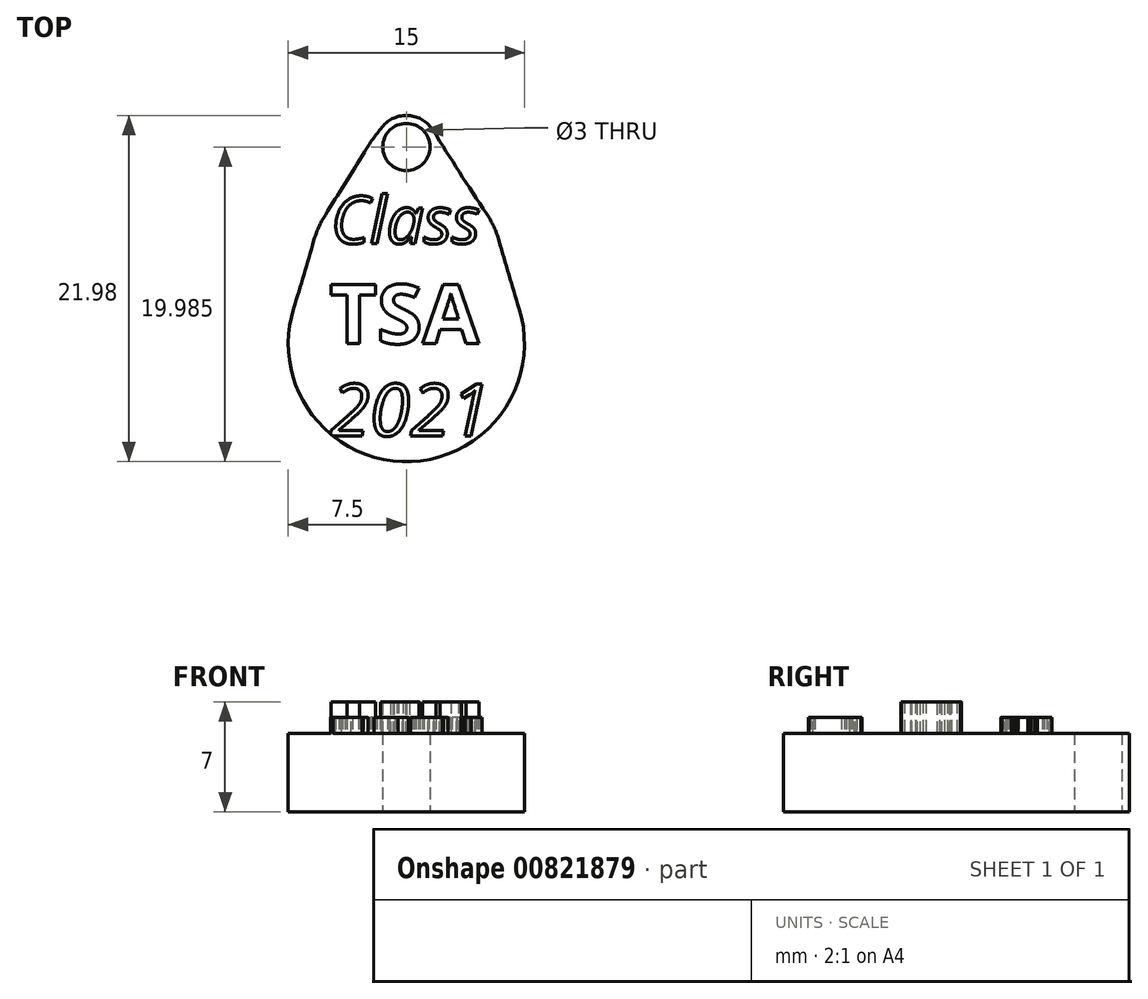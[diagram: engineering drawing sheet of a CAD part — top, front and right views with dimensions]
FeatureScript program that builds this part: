
annotation { "Feature Type Name" : "Feature", "Feature Type Description" : "" }
export const myFeature = defineFeature(function(context is Context, id is Id, definition is map)
    precondition{}
    {
        {
            var Q0;
            Q0=qCreatedBy(makeId("Top.planeOp"),FACE);
            var sketch = newSketch(context, id + "F0", { "sketchPlane" : qUnion([Q0])});
            skCircle(sketch, "E0", {"center": v(0, 0) * mm, "radius": 7.5 * mm});
            skText(sketch, "E1", { "text": "Class", "fontName": "OpenSans-Italic.ttf"});
            skLineSegment(sketch, "E2", {"start": v(-6.1, 4.38) * mm, "end": v(6.1, 4.38) * mm});
            skArc(sketch, "E3", {"start": v(6.1, 4.38) * mm, "mid": v(0, 10.98) * mm, "end": v(-6.1, 4.38) * mm});
            skCircle(sketch, "E4", {"center": v(0, 12.48) * mm, "radius": 1.5 * mm});
            skPoint(sketch, "E4.centerSnap0", {"position": v(0, 10.98) * mm});
            skCircle(sketch, "E5", {"center": v(0, 12.48) * mm, "radius": 2 * mm});
            skArc(sketch, "E6", {"start": v(-1.54, 13.76) * mm, "mid": v(-2.88, 11.78) * mm, "end": v(-3.87, 9.6) * mm});
            skLineSegment(sketch, "E7", {"start": v(0, 12.48) * mm, "end": v(0, 16.89) * mm});
            skArc(sketch, "E8.MirrorCS", {"start": v(1.54, 13.76) * mm, "mid": v(2.88, 11.78) * mm, "end": v(3.87, 9.6) * mm});
            skText(sketch, "E9", { "text": "2021", "fontName": "OpenSans-Italic.ttf"});
            const initialGuessF0  = {"E1": [-0.00479, 0.00635, 1, 0, 0.00302], "E9": [-0.00487, -0.00587, 1, 0, 0.00333]};
            skSetInitialGuess(sketch, initialGuessF0);
            skSolve(sketch);
        }
        {
            var Q0;
            {var subQ47=sQuery(id+"F0.wireOp",EDGE,"E1.sketch_text.stroke-5");Q0=makeQuery(id+"F0.imprint","IMPRINT",FACE,{"disambiguationData":[TD([[makeQuery(id+"F0.imprint","IMPRINT",EDGE,{"derivedFrom":subQ47}),1.0]])]});}
            var Q1;
            {var subQ0=sQuery(id+"F0.wireOp",EDGE,"4cedd241-6937-41b7-ad6b-732669d0c963.sketch_text.stroke-32");Q1=makeQuery(id+"F0.imprint","IMPRINT",FACE,{"disambiguationData":[TD([[makeQuery(id+"F0.imprint","IMPRINT",EDGE,{"derivedFrom":subQ0}),1.0]])]});}
            var Q2;
            {var subQ0=sQuery(id+"F0.wireOp",EDGE,"4cedd241-6937-41b7-ad6b-732669d0c963.sketch_text.stroke-5");Q2=makeQuery(id+"F0.imprint","IMPRINT",FACE,{"disambiguationData":[TD([[makeQuery(id+"F0.imprint","IMPRINT",EDGE,{"derivedFrom":subQ0}),1.0]])]});}
            var Q3;
            {var subQ21=sQuery(id+"F0.wireOp",EDGE,"4cedd241-6937-41b7-ad6b-732669d0c963.sketch_text.stroke-12");Q3=makeQuery(id+"F0.imprint","IMPRINT",FACE,{"disambiguationData":[TD([[makeQuery(id+"F0.imprint","IMPRINT",EDGE,{"derivedFrom":subQ21}),1.0]])]});}
            var Q4;
            Q4=makeQuery(id+"F0.imprint","IMPRINT",FACE,{"disambiguationData":[TD([[makeQuery(id+"F0.imprint","IMPRINT",EDGE,{"derivedFrom":sQuery(id+"F0.wireOp",EDGE,"E1.sketch_text.stroke-0")}),1.0]])]});
            var Q5;
            Q5=makeQuery(id+"F0.imprint","IMPRINT",FACE,{"disambiguationData":[TD([[makeQuery(id+"F0.imprint","IMPRINT",EDGE,{"derivedFrom":sQuery(id+"F0.wireOp",EDGE,"E1.sketch_text.stroke-36")}),1.0]])]});
            var Q6;
            {var subQ0=sQuery(id+"F0.wireOp",EDGE,"E1.sketch_text.stroke-39");Q6=makeQuery(id+"F0.imprint","IMPRINT",FACE,{"disambiguationData":[TD([[makeQuery(id+"F0.imprint","IMPRINT",EDGE,{"derivedFrom":subQ0}),1.0]])]});}
            var Q7;
            {var subQ0=sQuery(id+"F0.wireOp",EDGE,"E6");Q7=makeQuery(id+"F0.imprint","IMPRINT",FACE,{"disambiguationData":[TD([[makeQuery(id+"F0.imprint","IMPRINT",EDGE,{"derivedFrom":subQ0}),1.0]])]});}
            var Q8;
            {var subQ0=sQuery(id+"F0.wireOp",EDGE,"E8.MirrorCS");Q8=makeQuery(id+"F0.imprint","IMPRINT",FACE,{"disambiguationData":[TD([[makeQuery(id+"F0.imprint","IMPRINT",EDGE,{"derivedFrom":subQ0}),-1.0]])]});}
            var Q9;
            {var subQ0=sQuery(id+"F0.wireOp",EDGE,"E5");var subQ1=sQuery(id+"F0.wireOp",EDGE,"E3");var subQ2=makeQuery(id+"F0.imprint","INTERSECT",VERTEX,{"disambiguationData":[OD(0.0)],"derivedFrom":[subQ1,subQ0]});Q9=makeQuery(id+"F0.imprint","IMPRINT",FACE,{"disambiguationData":[TD([[makeQuery(id+"F0.imprint","IMPRINT",EDGE,{"disambiguationData":[TD([[subQ2,-1.0]])],"derivedFrom":subQ1}),1.0]])]});}
            var Q10;
            {var subQ0=sQuery(id+"F0.wireOp",EDGE,"E5");var subQ4=sQuery(id+"F0.wireOp",EDGE,"E3");var subQ5=makeQuery(id+"F0.imprint","INTERSECT",VERTEX,{"disambiguationData":[OD(0.0)],"derivedFrom":[subQ4,subQ0]});Q10=makeQuery(id+"F0.imprint","IMPRINT",FACE,{"disambiguationData":[TD([[makeQuery(id+"F0.imprint","IMPRINT",EDGE,{"disambiguationData":[TD([[subQ5,-1.0]])],"derivedFrom":subQ4}),-1.0]])]});}
            var Q11;
            {var subQ2=sQuery(id+"F0.wireOp",EDGE,"E3");var subQ6=sQuery(id+"F0.wireOp",EDGE,"E4");var subQ8=makeQuery(id+"F0.imprint","INTERSECT",VERTEX,{"derivedFrom":[subQ2,subQ6]});Q11=makeQuery(id+"F0.imprint","IMPRINT",FACE,{"disambiguationData":[TD([[makeQuery(id+"F0.imprint","IMPRINT",EDGE,{"disambiguationData":[TD([[subQ8,-1.0]])],"derivedFrom":subQ2}),-1.0]])]});}
            var Q12;
            {var subQ5=sQuery(id+"F0.wireOp",EDGE,"E2");Q12=makeQuery(id+"F0.imprint","IMPRINT",FACE,{"disambiguationData":[TD([[makeQuery(id+"F0.imprint","IMPRINT",EDGE,{"derivedFrom":subQ5}),-1.0]])]});}
            var Q13;
            Q13=makeQuery(id+"F0.imprint","IMPRINT",FACE,{"disambiguationData":[TD([[makeQuery(id+"F0.imprint","IMPRINT",EDGE,{"derivedFrom":sQuery(id+"F0.wireOp",EDGE,"E9.sketch_text.stroke-31")}),1.0]])]});
            extrude(context, id + "F1", {"entities" : qUnion([Q0, Q1, Q2, Q3, Q4, Q5, Q6, Q7, Q8, Q9, Q10, Q11, Q12, Q13]), "depth" : 5 * mm, "offsetDistance" : 25 * mm});
        }
        {
            var Q0;
            Q0=makeQuery(id+"F0.imprint","IMPRINT",FACE,{"disambiguationData":[TD([[makeQuery(id+"F0.imprint","IMPRINT",EDGE,{"derivedFrom":sQuery(id+"F0.wireOp",EDGE,"E1.sketch_text.stroke-21")}),-1.0]])]});
            var Q1;
            {var subQ10=sQuery(id+"F0.wireOp",EDGE,"E1.sketch_text.stroke-27");Q1=makeQuery(id+"F0.imprint","IMPRINT",FACE,{"disambiguationData":[TD([[makeQuery(id+"F0.imprint","IMPRINT",EDGE,{"derivedFrom":subQ10}),-1.0]])]});}
            var Q2;
            {var subQ5=sQuery(id+"F0.wireOp",EDGE,"E1.sketch_text.stroke-19");Q2=makeQuery(id+"F0.imprint","IMPRINT",FACE,{"disambiguationData":[TD([[makeQuery(id+"F0.imprint","IMPRINT",EDGE,{"derivedFrom":subQ5}),-1.0]])]});}
            var Q3;
            {var subQ5=sQuery(id+"F0.wireOp",EDGE,"E1.sketch_text.stroke-17");Q3=makeQuery(id+"F0.imprint","IMPRINT",FACE,{"disambiguationData":[TD([[makeQuery(id+"F0.imprint","IMPRINT",EDGE,{"derivedFrom":subQ5}),-1.0]])]});}
            var Q4;
            {var subQ0=sQuery(id+"F0.wireOp",EDGE,"E1.sketch_text.stroke-5");Q4=makeQuery(id+"F0.imprint","IMPRINT",FACE,{"disambiguationData":[TD([[makeQuery(id+"F0.imprint","IMPRINT",EDGE,{"derivedFrom":subQ0}),-1.0]])]});}
            var Q5;
            Q5=makeQuery(id+"F0.imprint","IMPRINT",FACE,{"disambiguationData":[TD([[makeQuery(id+"F0.imprint","IMPRINT",EDGE,{"derivedFrom":sQuery(id+"F0.wireOp",EDGE,"E1.sketch_text.stroke-0")}),-1.0]])]});
            var Q6;
            {var subQ2=sQuery(id+"F0.wireOp",EDGE,"E1.sketch_text.stroke-46");Q6=makeQuery(id+"F0.imprint","IMPRINT",FACE,{"disambiguationData":[TD([[makeQuery(id+"F0.imprint","IMPRINT",EDGE,{"derivedFrom":subQ2}),-1.0]])]});}
            var Q7;
            {var subQ6=sQuery(id+"F0.wireOp",EDGE,"E1.sketch_text.stroke-56");Q7=makeQuery(id+"F0.imprint","IMPRINT",FACE,{"disambiguationData":[TD([[makeQuery(id+"F0.imprint","IMPRINT",EDGE,{"derivedFrom":subQ6}),-1.0]])]});}
            var Q8;
            {var subQ0=sQuery(id+"F0.wireOp",EDGE,"E1.sketch_text.stroke-73");Q8=makeQuery(id+"F0.imprint","IMPRINT",FACE,{"disambiguationData":[TD([[makeQuery(id+"F0.imprint","IMPRINT",EDGE,{"derivedFrom":subQ0}),-1.0]])]});}
            var Q9;
            {var subQ6=sQuery(id+"F0.wireOp",EDGE,"E1.sketch_text.stroke-71");Q9=makeQuery(id+"F0.imprint","IMPRINT",FACE,{"disambiguationData":[TD([[makeQuery(id+"F0.imprint","IMPRINT",EDGE,{"derivedFrom":subQ6}),-1.0]])]});}
            var Q10;
            {var subQ5=sQuery(id+"F0.wireOp",EDGE,"E9.sketch_text.stroke-2");Q10=makeQuery(id+"F0.imprint","IMPRINT",FACE,{"disambiguationData":[TD([[makeQuery(id+"F0.imprint","IMPRINT",EDGE,{"derivedFrom":subQ5}),-1.0]])]});}
            var Q11;
            Q11=makeQuery(id+"F0.imprint","IMPRINT",FACE,{"disambiguationData":[TD([[makeQuery(id+"F0.imprint","IMPRINT",EDGE,{"derivedFrom":sQuery(id+"F0.wireOp",EDGE,"E9.sketch_text.stroke-22")}),-1.0]])]});
            var Q12;
            Q12=makeQuery(id+"F0.imprint","IMPRINT",FACE,{"disambiguationData":[TD([[makeQuery(id+"F0.imprint","IMPRINT",EDGE,{"derivedFrom":sQuery(id+"F0.wireOp",EDGE,"E9.sketch_text.stroke-40")}),-1.0]])]});
            var Q13;
            Q13=makeQuery(id+"F0.imprint","IMPRINT",FACE,{"disambiguationData":[TD([[makeQuery(id+"F0.imprint","IMPRINT",EDGE,{"derivedFrom":sQuery(id+"F0.wireOp",EDGE,"E9.sketch_text.stroke-62")}),-1.0]])]});
            extrude(context, id + "F2", {"entities" : qUnion([Q0, Q1, Q2, Q3, Q4, Q5, Q6, Q7, Q8, Q9, Q10, Q11, Q12, Q13]), "operationType" : NewBodyOperationType.ADD, "depth" : 6 * mm, "offsetDistance" : 25 * mm});
        }
        {
            var Q0;
            Q0=makeQuery(id+"F1.opExtrude","CAP_FACE",FACE,{"disambiguationData":[OSD([sQuery(id+"F0.wireOp",EDGE,"E0"),sQuery(id+"F0.wireOp",EDGE,"E1.sketch_text.stroke-0"),sQuery(id+"F0.wireOp",EDGE,"E1.sketch_text.stroke-1"),sQuery(id+"F0.wireOp",EDGE,"E1.sketch_text.stroke-2"),sQuery(id+"F0.wireOp",EDGE,"E1.sketch_text.stroke-3"),sQuery(id+"F0.wireOp",EDGE,"E1.sketch_text.stroke-4"),sQuery(id+"F0.wireOp",EDGE,"E1.sketch_text.stroke-5"),sQuery(id+"F0.wireOp",EDGE,"E1.sketch_text.stroke-6"),sQuery(id+"F0.wireOp",EDGE,"E1.sketch_text.stroke-7"),sQuery(id+"F0.wireOp",EDGE,"E1.sketch_text.stroke-8"),sQuery(id+"F0.wireOp",EDGE,"E1.sketch_text.stroke-9"),sQuery(id+"F0.wireOp",EDGE,"E1.sketch_text.stroke-10"),sQuery(id+"F0.wireOp",EDGE,"E1.sketch_text.stroke-11"),sQuery(id+"F0.wireOp",EDGE,"E1.sketch_text.stroke-12"),sQuery(id+"F0.wireOp",EDGE,"E1.sketch_text.stroke-13"),sQuery(id+"F0.wireOp",EDGE,"E1.sketch_text.stroke-14"),sQuery(id+"F0.wireOp",EDGE,"E1.sketch_text.stroke-15"),sQuery(id+"F0.wireOp",EDGE,"E1.sketch_text.stroke-16"),sQuery(id+"F0.wireOp",EDGE,"E1.sketch_text.stroke-17"),sQuery(id+"F0.wireOp",EDGE,"E1.sketch_text.stroke-18"),sQuery(id+"F0.wireOp",EDGE,"E1.sketch_text.stroke-19"),sQuery(id+"F0.wireOp",EDGE,"E1.sketch_text.stroke-20"),sQuery(id+"F0.wireOp",EDGE,"E1.sketch_text.stroke-21"),sQuery(id+"F0.wireOp",EDGE,"E1.sketch_text.stroke-22"),sQuery(id+"F0.wireOp",EDGE,"E1.sketch_text.stroke-23"),sQuery(id+"F0.wireOp",EDGE,"E1.sketch_text.stroke-24"),sQuery(id+"F0.wireOp",EDGE,"E1.sketch_text.stroke-25"),sQuery(id+"F0.wireOp",EDGE,"E1.sketch_text.stroke-26"),sQuery(id+"F0.wireOp",EDGE,"E1.sketch_text.stroke-27"),sQuery(id+"F0.wireOp",EDGE,"E1.sketch_text.stroke-28"),sQuery(id+"F0.wireOp",EDGE,"E1.sketch_text.stroke-29"),sQuery(id+"F0.wireOp",EDGE,"E1.sketch_text.stroke-30"),sQuery(id+"F0.wireOp",EDGE,"E1.sketch_text.stroke-31"),sQuery(id+"F0.wireOp",EDGE,"E1.sketch_text.stroke-32"),sQuery(id+"F0.wireOp",EDGE,"E1.sketch_text.stroke-33"),sQuery(id+"F0.wireOp",EDGE,"E1.sketch_text.stroke-34"),sQuery(id+"F0.wireOp",EDGE,"E1.sketch_text.stroke-35"),sQuery(id+"F0.wireOp",EDGE,"E1.sketch_text.stroke-46"),sQuery(id+"F0.wireOp",EDGE,"E1.sketch_text.stroke-47"),sQuery(id+"F0.wireOp",EDGE,"E1.sketch_text.stroke-48"),sQuery(id+"F0.wireOp",EDGE,"E1.sketch_text.stroke-49"),sQuery(id+"F0.wireOp",EDGE,"E1.sketch_text.stroke-50"),sQuery(id+"F0.wireOp",EDGE,"E1.sketch_text.stroke-51"),sQuery(id+"F0.wireOp",EDGE,"E1.sketch_text.stroke-52"),sQuery(id+"F0.wireOp",EDGE,"E1.sketch_text.stroke-53"),sQuery(id+"F0.wireOp",EDGE,"E1.sketch_text.stroke-54"),sQuery(id+"F0.wireOp",EDGE,"E1.sketch_text.stroke-55"),sQuery(id+"F0.wireOp",EDGE,"E1.sketch_text.stroke-56"),sQuery(id+"F0.wireOp",EDGE,"E1.sketch_text.stroke-57"),sQuery(id+"F0.wireOp",EDGE,"E1.sketch_text.stroke-58"),sQuery(id+"F0.wireOp",EDGE,"E1.sketch_text.stroke-59"),sQuery(id+"F0.wireOp",EDGE,"E1.sketch_text.stroke-60"),sQuery(id+"F0.wireOp",EDGE,"E1.sketch_text.stroke-61"),sQuery(id+"F0.wireOp",EDGE,"E1.sketch_text.stroke-62"),sQuery(id+"F0.wireOp",EDGE,"E1.sketch_text.stroke-63"),sQuery(id+"F0.wireOp",EDGE,"E1.sketch_text.stroke-64"),sQuery(id+"F0.wireOp",EDGE,"E1.sketch_text.stroke-65"),sQuery(id+"F0.wireOp",EDGE,"E1.sketch_text.stroke-66"),sQuery(id+"F0.wireOp",EDGE,"E1.sketch_text.stroke-67"),sQuery(id+"F0.wireOp",EDGE,"E1.sketch_text.stroke-68"),sQuery(id+"F0.wireOp",EDGE,"E1.sketch_text.stroke-69"),sQuery(id+"F0.wireOp",EDGE,"E1.sketch_text.stroke-70"),sQuery(id+"F0.wireOp",EDGE,"E1.sketch_text.stroke-71"),sQuery(id+"F0.wireOp",EDGE,"E1.sketch_text.stroke-72"),sQuery(id+"F0.wireOp",EDGE,"E1.sketch_text.stroke-73"),sQuery(id+"F0.wireOp",EDGE,"E1.sketch_text.stroke-74"),sQuery(id+"F0.wireOp",EDGE,"E1.sketch_text.stroke-75"),sQuery(id+"F0.wireOp",EDGE,"E1.sketch_text.stroke-76"),sQuery(id+"F0.wireOp",EDGE,"E1.sketch_text.stroke-77"),sQuery(id+"F0.wireOp",EDGE,"E1.sketch_text.stroke-78"),sQuery(id+"F0.wireOp",EDGE,"E1.sketch_text.stroke-79"),sQuery(id+"F0.wireOp",EDGE,"E1.sketch_text.stroke-80"),sQuery(id+"F0.wireOp",EDGE,"E1.sketch_text.stroke-81"),sQuery(id+"F0.wireOp",EDGE,"E1.sketch_text.stroke-82"),sQuery(id+"F0.wireOp",EDGE,"E1.sketch_text.stroke-83"),sQuery(id+"F0.wireOp",EDGE,"E1.sketch_text.stroke-84"),sQuery(id+"F0.wireOp",EDGE,"E1.sketch_text.stroke-85"),sQuery(id+"F0.wireOp",EDGE,"E1.sketch_text.stroke-86"),sQuery(id+"F0.wireOp",EDGE,"E1.sketch_text.stroke-87"),sQuery(id+"F0.wireOp",EDGE,"E1.sketch_text.stroke-88"),sQuery(id+"F0.wireOp",EDGE,"E1.sketch_text.stroke-89"),sQuery(id+"F0.wireOp",EDGE,"E1.sketch_text.stroke-90"),sQuery(id+"F0.wireOp",EDGE,"E1.sketch_text.stroke-91"),sQuery(id+"F0.wireOp",EDGE,"E1.sketch_text.stroke-92"),sQuery(id+"F0.wireOp",EDGE,"E1.sketch_text.stroke-93"),sQuery(id+"F0.wireOp",EDGE,"E1.sketch_text.stroke-94"),sQuery(id+"F0.wireOp",EDGE,"E1.sketch_text.stroke-95"),sQuery(id+"F0.wireOp",EDGE,"4cedd241-6937-41b7-ad6b-732669d0c963.sketch_text.stroke-11"),sQuery(id+"F0.wireOp",EDGE,"4cedd241-6937-41b7-ad6b-732669d0c963.sketch_text.stroke-12"),sQuery(id+"F0.wireOp",EDGE,"4cedd241-6937-41b7-ad6b-732669d0c963.sketch_text.stroke-13"),sQuery(id+"F0.wireOp",EDGE,"4cedd241-6937-41b7-ad6b-732669d0c963.sketch_text.stroke-14"),sQuery(id+"F0.wireOp",EDGE,"4cedd241-6937-41b7-ad6b-732669d0c963.sketch_text.stroke-15"),sQuery(id+"F0.wireOp",EDGE,"4cedd241-6937-41b7-ad6b-732669d0c963.sketch_text.stroke-20"),sQuery(id+"F0.wireOp",EDGE,"4cedd241-6937-41b7-ad6b-732669d0c963.sketch_text.stroke-23"),sQuery(id+"F0.wireOp",EDGE,"4cedd241-6937-41b7-ad6b-732669d0c963.sketch_text.stroke-24"),sQuery(id+"F0.wireOp",EDGE,"4cedd241-6937-41b7-ad6b-732669d0c963.sketch_text.stroke-25"),sQuery(id+"F0.wireOp",EDGE,"4cedd241-6937-41b7-ad6b-732669d0c963.sketch_text.stroke-26"),sQuery(id+"F0.wireOp",EDGE,"4cedd241-6937-41b7-ad6b-732669d0c963.sketch_text.stroke-27"),sQuery(id+"F0.wireOp",EDGE,"4cedd241-6937-41b7-ad6b-732669d0c963.sketch_text.stroke-39"),sQuery(id+"F0.wireOp",EDGE,"4cedd241-6937-41b7-ad6b-732669d0c963.sketch_text.stroke-40"),sQuery(id+"F0.wireOp",EDGE,"4cedd241-6937-41b7-ad6b-732669d0c963.sketch_text.stroke-41"),sQuery(id+"F0.wireOp",EDGE,"4cedd241-6937-41b7-ad6b-732669d0c963.sketch_text.stroke-42"),sQuery(id+"F0.wireOp",EDGE,"4cedd241-6937-41b7-ad6b-732669d0c963.sketch_text.stroke-43"),sQuery(id+"F0.wireOp",EDGE,"4cedd241-6937-41b7-ad6b-732669d0c963.sketch_text.stroke-44"),sQuery(id+"F0.wireOp",EDGE,"4cedd241-6937-41b7-ad6b-732669d0c963.sketch_text.stroke-45"),sQuery(id+"F0.wireOp",EDGE,"4cedd241-6937-41b7-ad6b-732669d0c963.sketch_text.stroke-46"),sQuery(id+"F0.wireOp",EDGE,"4cedd241-6937-41b7-ad6b-732669d0c963.sketch_text.stroke-47"),sQuery(id+"F0.wireOp",EDGE,"4cedd241-6937-41b7-ad6b-732669d0c963.sketch_text.stroke-48"),sQuery(id+"F0.wireOp",EDGE,"4cedd241-6937-41b7-ad6b-732669d0c963.sketch_text.stroke-49"),sQuery(id+"F0.wireOp",EDGE,"4cedd241-6937-41b7-ad6b-732669d0c963.sketch_text.stroke-50"),sQuery(id+"F0.wireOp",EDGE,"4cedd241-6937-41b7-ad6b-732669d0c963.sketch_text.stroke-51"),sQuery(id+"F0.wireOp",EDGE,"4cedd241-6937-41b7-ad6b-732669d0c963.sketch_text.stroke-58"),sQuery(id+"F0.wireOp",EDGE,"4cedd241-6937-41b7-ad6b-732669d0c963.sketch_text.stroke-59"),sQuery(id+"F0.wireOp",EDGE,"4cedd241-6937-41b7-ad6b-732669d0c963.sketch_text.stroke-60"),sQuery(id+"F0.wireOp",EDGE,"4cedd241-6937-41b7-ad6b-732669d0c963.sketch_text.stroke-61"),sQuery(id+"F0.wireOp",EDGE,"4cedd241-6937-41b7-ad6b-732669d0c963.sketch_text.stroke-62"),sQuery(id+"F0.wireOp",EDGE,"4cedd241-6937-41b7-ad6b-732669d0c963.sketch_text.stroke-63"),sQuery(id+"F0.wireOp",EDGE,"4cedd241-6937-41b7-ad6b-732669d0c963.sketch_text.stroke-64"),sQuery(id+"F0.wireOp",EDGE,"E3")])],"isStart":false});
            var sketch = newSketch(context, id + "F3", { "sketchPlane" : qUnion([Q0])});
            skText(sketch, "E10", { "text": "TSA", "fontName": "OpenSans-Bold.ttf"});
            const initialGuessF3  = {"E10": [-0.0049, 0, 1, 0, 0.00377]};
            skSetInitialGuess(sketch, initialGuessF3);
            skSolve(sketch);
        }
        {
            var Q0;
            Q0 = qSketchRegion(id + "F3", true);
            extrude(context, id + "F4", {"entities" : qUnion([Q0]), "operationType" : NewBodyOperationType.ADD, "depth" : 2 * mm, "offsetDistance" : 25 * mm});
        }
        {
            var Q0;
            {var subQ0=sQuery(id+"F0.wireOp",EDGE,"E3");var subQ1=sQuery(id+"F0.wireOp",EDGE,"E2");var subQ2=sQuery(id+"F0.wireOp",EDGE,"E0");Q0=makeQuery(id+"F1.opExtrude","SWEPT_EDGE",EDGE,{"disambiguationData":[OSD([subQ2,subQ1,subQ0]),TDD([makeQuery(id+"F0.imprint","INTERSECT",VERTEX,{"disambiguationData":[OD(1.0)],"derivedFrom":[subQ2,subQ1,subQ0]})])]});}
            var Q1;
            {var subQ0=sQuery(id+"F0.wireOp",EDGE,"E3");var subQ1=sQuery(id+"F0.wireOp",EDGE,"E2");var subQ2=sQuery(id+"F0.wireOp",EDGE,"E0");Q1=makeQuery(id+"F1.opExtrude","SWEPT_EDGE",EDGE,{"disambiguationData":[OSD([subQ2,subQ1,subQ0]),TDD([makeQuery(id+"F0.imprint","INTERSECT",VERTEX,{"disambiguationData":[OD(0.0)],"derivedFrom":[subQ2,subQ1,subQ0]})])]});}
            fillet(context, id + "F5", {"entities" : qUnion([Q0, Q1]), "radius" : 159 * mm, "tangentPropagation" : true, "allowEdgeOverflow" : false});
        }
        {
            var Q0;
            Q0=makeQuery(id+"F1.opExtrude","SWEPT_EDGE",EDGE,{"disambiguationData":[OSD([sQuery(id+"F0.wireOp",EDGE,"E3"),sQuery(id+"F0.wireOp",EDGE,"E6")])]});
            var Q1;
            Q1=makeQuery(id+"F1.opExtrude","SWEPT_EDGE",EDGE,{"disambiguationData":[OSD([sQuery(id+"F0.wireOp",EDGE,"E3"),sQuery(id+"F0.wireOp",EDGE,"E8.MirrorCS")])]});
            fillet(context, id + "F6", {"entities" : qUnion([Q0, Q1]), "radius" : 180.17 * mm, "tangentPropagation" : true, "allowEdgeOverflow" : false});
        }
    });
